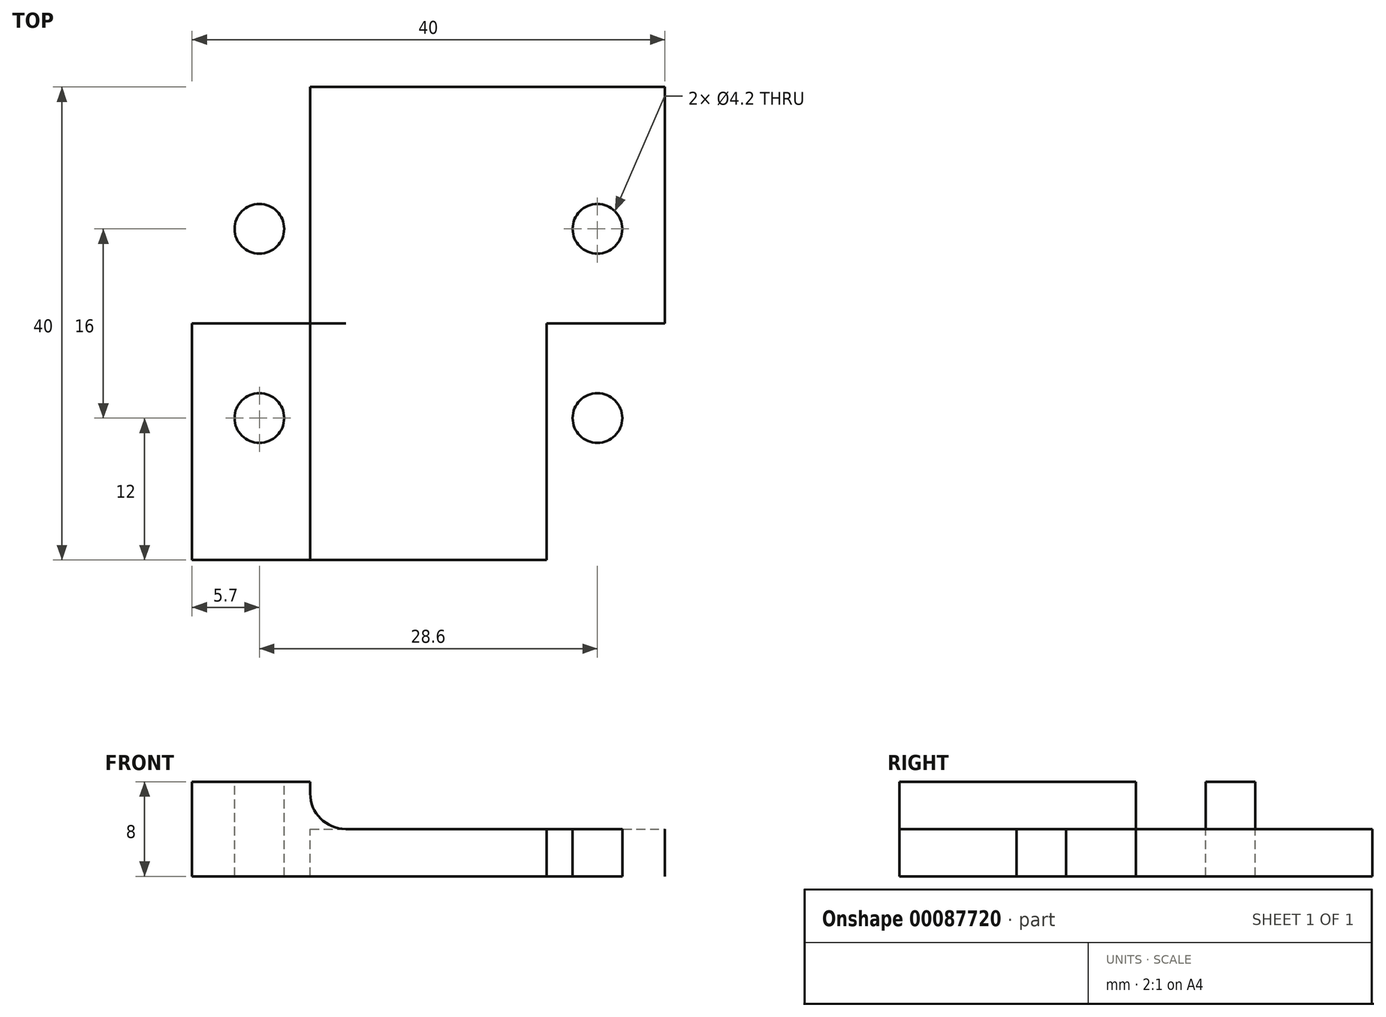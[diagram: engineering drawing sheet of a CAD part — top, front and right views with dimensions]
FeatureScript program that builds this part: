
annotation { "Feature Type Name" : "Feature", "Feature Type Description" : "" }
export const myFeature = defineFeature(function(context is Context, id is Id, definition is map)
    precondition{}
    {
        {
            var Q0;
            Q0=qCreatedBy(makeId("Top.planeOp"),FACE);
            var sketch = newSketch(context, id + "F0", { "sketchPlane" : qUnion([Q0])});
            skLineSegment(sketch, "E0.bottom", {"start": v(0, 0) * mm, "end": v(40, 0) * mm});
            skLineSegment(sketch, "E0.top", {"start": v(0, 40) * mm, "end": v(40, 40) * mm});
            skLineSegment(sketch, "E0.left", {"start": v(0, 0) * mm, "end": v(0, 40) * mm});
            skLineSegment(sketch, "E0.right", {"start": v(40, 0) * mm, "end": v(40, 40) * mm});
            skSolve(sketch);
        }
        {
            var Q0;
            Q0=makeQuery(id+"F0.imprint","IMPRINT",FACE,{"disambiguationData":[TD([[makeQuery(id+"F0.imprint","IMPRINT",EDGE,{"derivedFrom":sQuery(id+"F0.wireOp",EDGE,"E0.bottom")}),1.0]])]});
            extrude(context, id + "F1", {"entities" : qUnion([Q0]), "depth" : 8 * mm});
        }
        {
            var Q0;
            Q0=makeQuery(id+"F1.opExtrude","CAP_FACE",FACE,{"disambiguationData":[OSD([sQuery(id+"F0.wireOp",EDGE,"E0.bottom"),sQuery(id+"F0.wireOp",EDGE,"E0.top"),sQuery(id+"F0.wireOp",EDGE,"E0.left"),sQuery(id+"F0.wireOp",EDGE,"E0.right")])],"isStart":false});
            var sketch = newSketch(context, id + "F2", { "sketchPlane" : qUnion([Q0])});
            skLineSegment(sketch, "E1", {"start": v(20, 40) * mm, "end": v(20, 0) * mm});
            skLineSegment(sketch, "E2", {"start": v(20, 0) * mm, "end": v(30, 0) * mm});
            skLineSegment(sketch, "E3", {"start": v(20, 0) * mm, "end": v(10, 0) * mm});
            skLineSegment(sketch, "E4", {"start": v(10, 0) * mm, "end": v(10, 40) * mm});
            skLineSegment(sketch, "E5", {"start": v(30, 0) * mm, "end": v(30, 40) * mm});
            skLineSegment(sketch, "E6", {"start": v(10, 40) * mm, "end": v(10, 28) * mm});
            skLineSegment(sketch, "E7", {"start": v(10, 0) * mm, "end": v(10, 12) * mm});
            skLineSegment(sketch, "E8", {"start": v(10, 12) * mm, "end": v(5.7, 12) * mm});
            skCircle(sketch, "E9", {"center": v(5.7, 12) * mm, "radius": 2.1 * mm});
            skLineSegment(sketch, "E10", {"start": v(10, 28) * mm, "end": v(5.7, 28) * mm});
            skLineSegment(sketch, "E11", {"start": v(0, 20) * mm, "end": v(40, 20) * mm});
            skCircle(sketch, "E12.MirrorC", {"center": v(5.7, 28) * mm, "radius": 2.1 * mm});
            skCircle(sketch, "E13.MirrorC", {"center": v(34.3, 28) * mm, "radius": 2.1 * mm});
            skCircle(sketch, "E14.MirrorC", {"center": v(34.3, 12) * mm, "radius": 2.1 * mm});
            skSolve(sketch);
        }
        {
            var Q0;
            Q0=makeQuery(id+"F2.imprint","IMPRINT",FACE,{"disambiguationData":[TD([[makeQuery(id+"F2.imprint","IMPRINT",EDGE,{"derivedFrom":sQuery(id+"F2.wireOp",EDGE,"7p7YwOhI-lxlm-OVLn-esk2-DzV9JAAtHLwd")}),1.0]])]});
            var Q1;
            Q1=makeQuery(id+"F2.imprint","IMPRINT",FACE,{"disambiguationData":[TD([[makeQuery(id+"F2.imprint","IMPRINT",EDGE,{"derivedFrom":sQuery(id+"F2.wireOp",EDGE,"E9")}),1.0]])]});
            var Q2;
            Q2=makeQuery(id+"F2.imprint","IMPRINT",FACE,{"disambiguationData":[TD([[makeQuery(id+"F2.imprint","IMPRINT",EDGE,{"derivedFrom":sQuery(id+"F2.wireOp",EDGE,"84b2104a-56fc-49e7-88ef-069794ee41bf1.MirrorC")}),-1.0]])]});
            var Q3;
            Q3=makeQuery(id+"F2.imprint","IMPRINT",FACE,{"disambiguationData":[TD([[makeQuery(id+"F2.imprint","IMPRINT",EDGE,{"derivedFrom":sQuery(id+"F2.wireOp",EDGE,"84b2104a-56fc-49e7-88ef-069794ee41bf0.MirrorC")}),-1.0]])]});
            var Q4;
            Q4=makeQuery(id+"F2.imprint","IMPRINT",FACE,{"disambiguationData":[TD([[makeQuery(id+"F2.imprint","IMPRINT",EDGE,{"derivedFrom":sQuery(id+"F2.wireOp",EDGE,"E12.MirrorC")}),-1.0]])]});
            var Q5;
            Q5=makeQuery(id+"F2.imprint","IMPRINT",FACE,{"disambiguationData":[TD([[makeQuery(id+"F2.imprint","IMPRINT",EDGE,{"derivedFrom":sQuery(id+"F2.wireOp",EDGE,"E13.MirrorC")}),1.0]])]});
            var Q6;
            Q6=makeQuery(id+"F2.imprint","IMPRINT",FACE,{"disambiguationData":[TD([[makeQuery(id+"F2.imprint","IMPRINT",EDGE,{"derivedFrom":sQuery(id+"F2.wireOp",EDGE,"E14.MirrorC")}),-1.0]])]});
            extrude(context, id + "F3", {"entities" : qUnion([Q0, Q1, Q2, Q3, Q4, Q5, Q6]), "operationType" : NewBodyOperationType.REMOVE, "oppositeDirection" : true, "depth" : 25 * mm});
        }
        {
            var Q0;
            Q0=makeQuery(id+"F1.opExtrude","SWEPT_FACE",FACE,{"disambiguationData":[OSD([sQuery(id+"F0.wireOp",EDGE,"E0.top")])]});
            var sketch = newSketch(context, id + "F4", { "sketchPlane" : qUnion([Q0])});
            skLineSegment(sketch, "E15", {"start": v(0, 4) * mm, "end": v(-40, 4) * mm});
            skSolve(sketch);
        }
        {
            var Q0;
            {var subQ0=sQuery(id+"F4.wireOp",EDGE,"E15");Q0=makeQuery(id+"F4.imprint","IMPRINT",FACE,{"disambiguationData":[TD([[makeQuery(id+"F4.imprint","IMPRINT",EDGE,{"derivedFrom":subQ0}),-1.0]])]});}
            extrude(context, id + "F5", {"entities" : qUnion([Q0]), "operationType" : NewBodyOperationType.REMOVE, "oppositeDirection" : true, "depth" : 100 * mm});
        }
        {
            var Q0;
            Q0=makeQuery(id+"F5.boolean.opBoolean","COPY",EDGE,{"derivedFrom":makeQuery(id+"F5.opExtrude","SWEPT_EDGE",EDGE,{"disambiguationData":[OSD([sQuery(id+"F0.wireOp",EDGE,"E0.top"),sQuery(id+"F0.wireOp",EDGE,"E0.left"),sQuery(id+"F4.wireOp",EDGE,"E15")])]})});
            var Q1;
            Q1=makeQuery(id+"F5.boolean.opBoolean","COPY",EDGE,{"derivedFrom":makeQuery(id+"F5.opExtrude","SWEPT_EDGE",EDGE,{"disambiguationData":[OSD([sQuery(id+"F0.wireOp",EDGE,"E0.top"),sQuery(id+"F0.wireOp",EDGE,"E0.right"),sQuery(id+"F4.wireOp",EDGE,"E15")])]})});
            fillet(context, id + "F6", {"entities" : qUnion([Q0, Q1]), "radius" : 3 * mm, "tangentPropagation" : true, "allowEdgeOverflow" : false});
        }
    });
